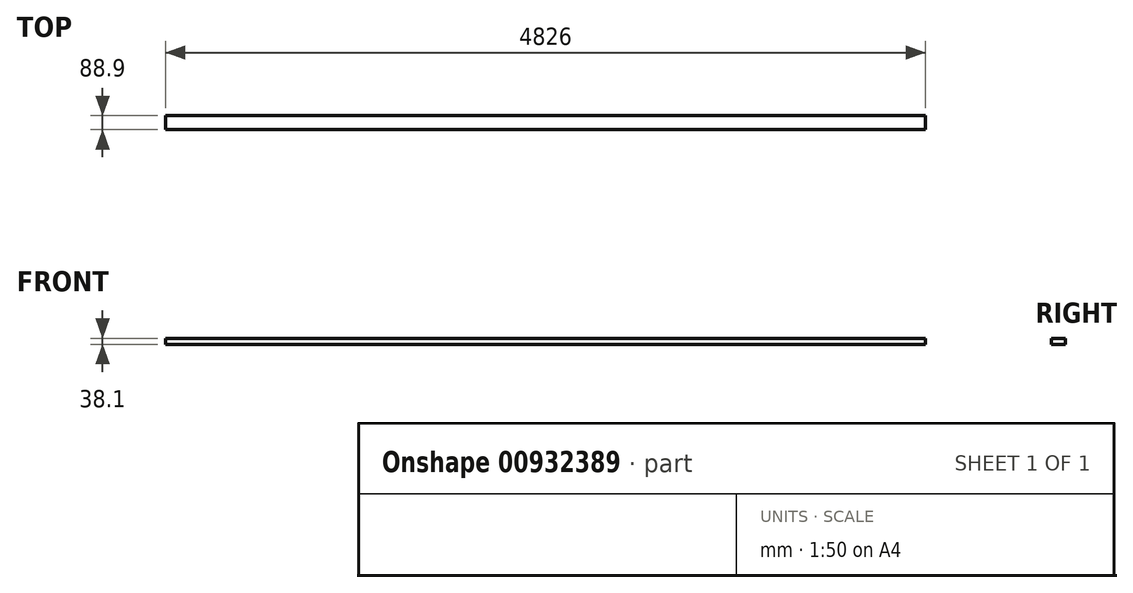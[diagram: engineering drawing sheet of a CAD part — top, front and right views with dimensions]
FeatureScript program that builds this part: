
annotation { "Feature Type Name" : "Feature", "Feature Type Description" : "" }
export const myFeature = defineFeature(function(context is Context, id is Id, definition is map)
    precondition{}
    {
        {
            var Q0;
            Q0=qCreatedBy(makeId("Right.planeOp"),FACE);
            var sketch = newSketch(context, id + "F0", { "sketchPlane" : qUnion([Q0])});
            skLineSegment(sketch, "E0.bottom", {"start": v(44.45, 19.05) * mm, "end": v(-44.45, 19.05) * mm});
            skLineSegment(sketch, "E0.top", {"start": v(44.45, -19.05) * mm, "end": v(-44.45, -19.05) * mm});
            skLineSegment(sketch, "E0.left", {"start": v(44.45, 19.05) * mm, "end": v(44.45, -19.05) * mm});
            skLineSegment(sketch, "E0.right", {"start": v(-44.45, 19.05) * mm, "end": v(-44.45, -19.05) * mm});
            skPoint(sketch, "E0.middle", {"position": v(0, 0) * mm});
            skSolve(sketch);
        }
        {
            var Q0;
            Q0=makeQuery(id+"F0.imprint","IMPRINT",FACE,{"disambiguationData":[TD([[makeQuery(id+"F0.imprint","IMPRINT",EDGE,{"derivedFrom":sQuery(id+"F0.wireOp",EDGE,"E0.bottom")}),1.0]])]});
            extrude(context, id + "F1", {"entities" : qUnion([Q0]), "depth" : 4826 * mm, "offsetDistance" : 25.4 * mm});
        }
    });
